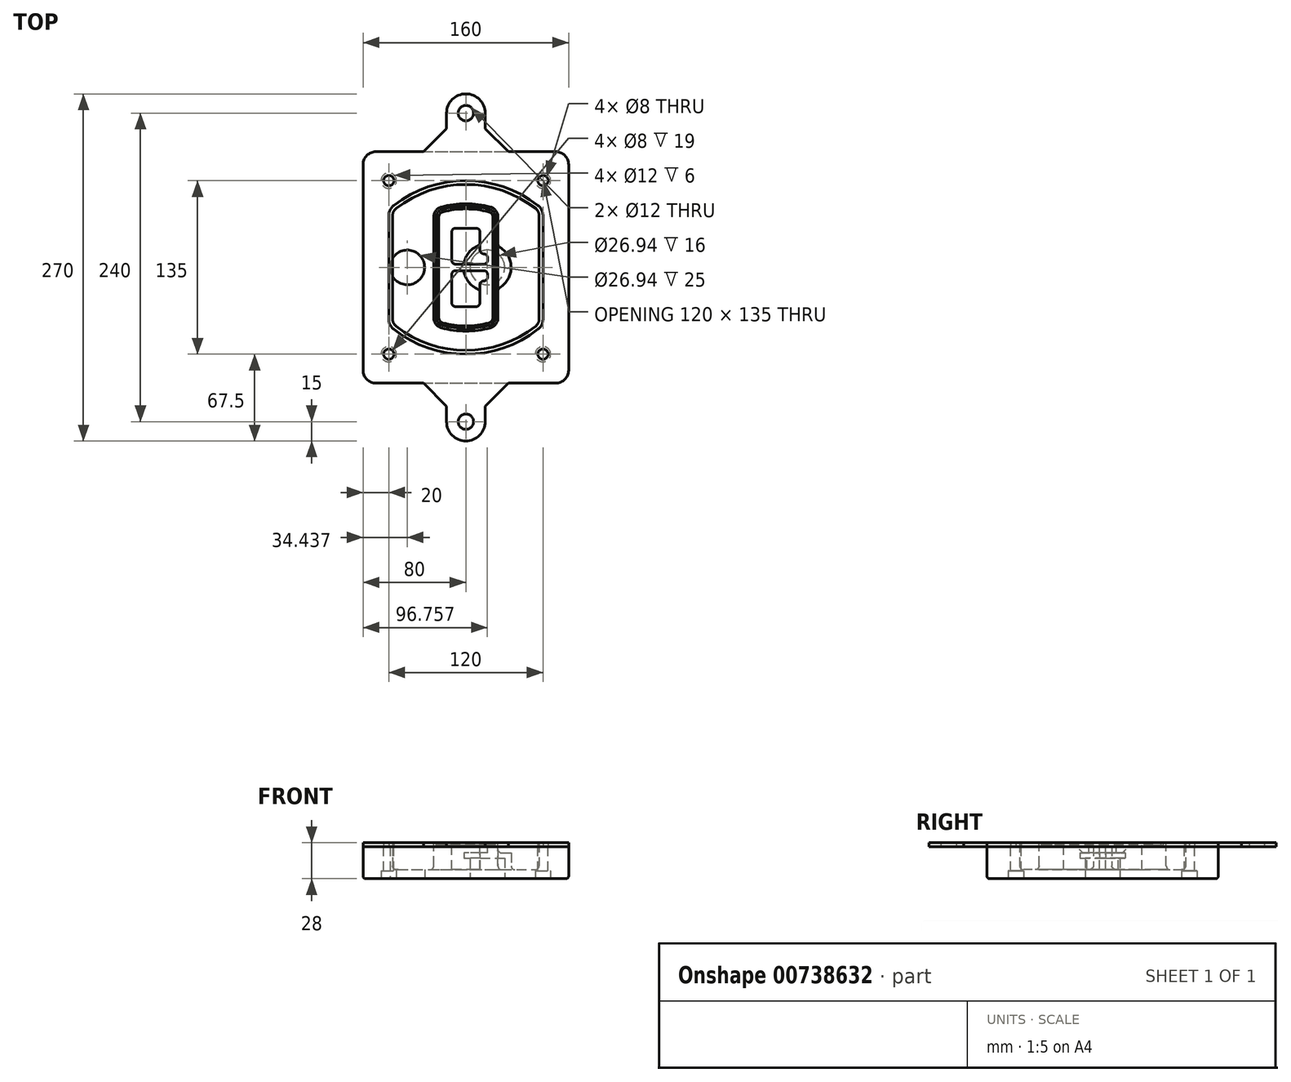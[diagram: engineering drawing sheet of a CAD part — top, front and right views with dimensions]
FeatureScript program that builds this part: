
annotation { "Feature Type Name" : "Feature", "Feature Type Description" : "" }
export const myFeature = defineFeature(function(context is Context, id is Id, definition is map)
    precondition{}
    {
        {
            var Q0;
            Q0=qCreatedBy(makeId("Top.planeOp"),FACE);
            var sketch = newSketch(context, id + "F0", { "sketchPlane" : qUnion([Q0])});
            skPoint(sketch, "E0.rect.middle", {"position": v(0, 0) * mm});
            skLineSegment(sketch, "E1.bottom", {"start": v(-70, -90) * mm, "end": v(70, -90) * mm});
            skLineSegment(sketch, "E1.top", {"start": v(-70, 90) * mm, "end": v(70, 90) * mm});
            skLineSegment(sketch, "E1.left", {"start": v(-80, -80) * mm, "end": v(-80, 80) * mm});
            skLineSegment(sketch, "E1.right", {"start": v(80, -80) * mm, "end": v(80, 80) * mm});
            skLineSegment(sketch, "E2", {"start": v(-80, 90) * mm, "end": v(80, -90) * mm, "construction": true});
            skLineSegment(sketch, "E3", {"start": v(80, 90) * mm, "end": v(-80, -90) * mm, "construction": true});
            skCircle(sketch, "E4", {"center": v(-60, 67.5) * mm, "radius": 4 * mm});
            skCircle(sketch, "E5", {"center": v(60, 67.5) * mm, "radius": 4 * mm});
            skCircle(sketch, "E6", {"center": v(60, -67.5) * mm, "radius": 4 * mm});
            skCircle(sketch, "E7", {"center": v(-60, -67.5) * mm, "radius": 4 * mm});
            skLineSegment(sketch, "E8", {"start": v(-60, 67.5) * mm, "end": v(60, 67.5) * mm, "construction": true});
            skLineSegment(sketch, "E9", {"start": v(60, 67.5) * mm, "end": v(60, -67.5) * mm, "construction": true});
            skLineSegment(sketch, "E10", {"start": v(60, -67.5) * mm, "end": v(-60, -67.5) * mm, "construction": true});
            skLineSegment(sketch, "E11", {"start": v(-60, -67.5) * mm, "end": v(-60, 67.5) * mm, "construction": true});
            skLineSegment(sketch, "E12", {"start": v(-60, 40.3) * mm, "end": v(-60, -40.3) * mm});
            skLineSegment(sketch, "E13", {"start": v(60, 40.3) * mm, "end": v(60, -40.3) * mm});
            skArc(sketch, "E14", {"start": v(56.15, 48.18) * mm, "mid": v(0, 67.5) * mm, "end": v(-56.15, 48.18) * mm});
            skArc(sketch, "E15", {"start": v(-56.15, -48.18) * mm, "mid": v(0, -67.5) * mm, "end": v(56.15, -48.18) * mm});
            skLineSegment(sketch, "E16", {"start": v(-60, 0) * mm, "end": v(60, 0) * mm, "construction": true});
            skPoint(sketch, "E17.visualSharp", {"position": v(-60, -45) * mm});
            skArc(sketch, "E17.filletArc", {"start": v(-60, -40.3) * mm, "mid": v(-58.99, -44.68) * mm, "end": v(-56.15, -48.18) * mm});
            skPoint(sketch, "E18.visualSharp", {"position": v(-60, 45) * mm});
            skArc(sketch, "E18.filletArc", {"start": v(-56.15, 48.18) * mm, "mid": v(-58.99, 44.68) * mm, "end": v(-60, 40.3) * mm});
            skPoint(sketch, "E19.visualSharp", {"position": v(60, 45) * mm});
            skArc(sketch, "E19.filletArc", {"start": v(60, 40.3) * mm, "mid": v(58.99, 44.68) * mm, "end": v(56.15, 48.18) * mm});
            skPoint(sketch, "E20.visualSharp", {"position": v(60, -45) * mm});
            skArc(sketch, "E20.filletArc", {"start": v(56.15, -48.18) * mm, "mid": v(58.99, -44.68) * mm, "end": v(60, -40.3) * mm});
            skPoint(sketch, "E21.visualSharp", {"position": v(-80, 90) * mm});
            skArc(sketch, "E21.filletArc", {"start": v(-70, 90) * mm, "mid": v(-77.07, 87.07) * mm, "end": v(-80, 80) * mm});
            skPoint(sketch, "E22.visualSharp", {"position": v(80, 90) * mm});
            skArc(sketch, "E22.filletArc", {"start": v(80, 80) * mm, "mid": v(77.07, 87.07) * mm, "end": v(70, 90) * mm});
            skPoint(sketch, "E23.visualSharp", {"position": v(80, -90) * mm});
            skArc(sketch, "E23.filletArc", {"start": v(70, -90) * mm, "mid": v(77.07, -87.07) * mm, "end": v(80, -80) * mm});
            skPoint(sketch, "E24.visualSharp", {"position": v(-80, -90) * mm});
            skArc(sketch, "E24.filletArc", {"start": v(-80, -80) * mm, "mid": v(-77.07, -87.07) * mm, "end": v(-70, -90) * mm});
            skArc(sketch, "E25.0", {"start": v(57, 40.3) * mm, "mid": v(56.3, 43.36) * mm, "end": v(54.3, 45.81) * mm});
            skLineSegment(sketch, "E25.1", {"start": v(57, 40.3) * mm, "end": v(57, -40.3) * mm});
            skArc(sketch, "E25.2", {"start": v(54.3, -45.81) * mm, "mid": v(56.3, -43.36) * mm, "end": v(57, -40.3) * mm});
            skArc(sketch, "E25.3", {"start": v(-54.3, -45.81) * mm, "mid": v(0, -64.5) * mm, "end": v(54.3, -45.81) * mm});
            skArc(sketch, "E25.4", {"start": v(-57, -40.3) * mm, "mid": v(-56.3, -43.36) * mm, "end": v(-54.3, -45.81) * mm});
            skArc(sketch, "E25.5", {"start": v(54.3, 45.81) * mm, "mid": v(0, 64.5) * mm, "end": v(-54.3, 45.81) * mm});
            skLineSegment(sketch, "E25.6", {"start": v(-57, 40.3) * mm, "end": v(-57, -40.3) * mm});
            skArc(sketch, "E25.7", {"start": v(-54.3, 45.81) * mm, "mid": v(-56.3, 43.36) * mm, "end": v(-57, 40.3) * mm});
            skArc(sketch, "E26.0", {"start": v(-58.62, 51.33) * mm, "mid": v(-62.58, 46.43) * mm, "end": v(-64, 40.3) * mm});
            skArc(sketch, "E26.1", {"start": v(58.62, 51.33) * mm, "mid": v(0, 71.5) * mm, "end": v(-58.62, 51.33) * mm});
            skArc(sketch, "E26.2", {"start": v(64, 40.3) * mm, "mid": v(62.58, 46.43) * mm, "end": v(58.62, 51.33) * mm});
            skLineSegment(sketch, "E26.3", {"start": v(64, 40.3) * mm, "end": v(64, -40.3) * mm});
            skArc(sketch, "E26.4", {"start": v(58.62, -51.33) * mm, "mid": v(62.58, -46.43) * mm, "end": v(64, -40.3) * mm});
            skLineSegment(sketch, "E26.5", {"start": v(-64, 40.3) * mm, "end": v(-64, -40.3) * mm});
            skArc(sketch, "E26.6", {"start": v(-58.62, -51.33) * mm, "mid": v(0, -71.5) * mm, "end": v(58.62, -51.33) * mm});
            skArc(sketch, "E26.7", {"start": v(-64, -40.3) * mm, "mid": v(-62.58, -46.43) * mm, "end": v(-58.62, -51.33) * mm});
            skSolve(sketch);
        }
        {
            var Q0;
            Q0=makeQuery(id+"F0.imprint","IMPRINT",FACE,{"disambiguationData":[TD([[makeQuery(id+"F0.imprint","IMPRINT",EDGE,{"derivedFrom":sQuery(id+"F0.wireOp",EDGE,"E1.bottom")}),1.0]])]});
            var Q1;
            Q1=makeQuery(id+"F0.imprint","IMPRINT",FACE,{"disambiguationData":[TD([[makeQuery(id+"F0.imprint","IMPRINT",EDGE,{"derivedFrom":sQuery(id+"F0.wireOp",EDGE,"E12")}),1.0]])]});
            var Q2;
            Q2=makeQuery(id+"F0.imprint","IMPRINT",FACE,{"disambiguationData":[TD([[makeQuery(id+"F0.imprint","IMPRINT",EDGE,{"derivedFrom":sQuery(id+"F0.wireOp",EDGE,"E25.0")}),1.0]])]});
            var Q3;
            Q3=makeQuery(id+"F0.imprint","IMPRINT",FACE,{"disambiguationData":[TD([[makeQuery(id+"F0.imprint","IMPRINT",EDGE,{"derivedFrom":sQuery(id+"F0.wireOp",EDGE,"E12")}),-1.0]])]});
            extrude(context, id + "F1", {"entities" : qUnion([Q0, Q1, Q2, Q3]), "oppositeDirection" : true, "depth" : 25 * mm});
        }
        {
            var Q0;
            Q0=makeQuery(id+"F0.imprint","IMPRINT",FACE,{"disambiguationData":[TD([[makeQuery(id+"F0.imprint","IMPRINT",EDGE,{"derivedFrom":sQuery(id+"F0.wireOp",EDGE,"E12")}),1.0]])]});
            extrude(context, id + "F2", {"entities" : qUnion([Q0]), "operationType" : NewBodyOperationType.ADD, "depth" : 3 * mm});
        }
        {
            var Q0;
            Q0=makeQuery(id+"F0.imprint","IMPRINT",FACE,{"disambiguationData":[TD([[makeQuery(id+"F0.imprint","IMPRINT",EDGE,{"derivedFrom":sQuery(id+"F0.wireOp",EDGE,"E25.0")}),1.0]])]});
            extrude(context, id + "F3", {"entities" : qUnion([Q0]), "operationType" : NewBodyOperationType.REMOVE, "oppositeDirection" : true, "depth" : 18 * mm});
        }
        {
            var Q0;
            Q0=makeQuery(id+"F2.opExtrude","CAP_FACE",FACE,{"disambiguationData":[OSD([sQuery(id+"F0.wireOp",EDGE,"E12"),sQuery(id+"F0.wireOp",EDGE,"E13"),sQuery(id+"F0.wireOp",EDGE,"E14"),sQuery(id+"F0.wireOp",EDGE,"E15"),sQuery(id+"F0.wireOp",EDGE,"E17.filletArc"),sQuery(id+"F0.wireOp",EDGE,"E18.filletArc"),sQuery(id+"F0.wireOp",EDGE,"E19.filletArc"),sQuery(id+"F0.wireOp",EDGE,"E20.filletArc"),sQuery(id+"F0.wireOp",EDGE,"E25.0"),sQuery(id+"F0.wireOp",EDGE,"E25.1"),sQuery(id+"F0.wireOp",EDGE,"E25.2"),sQuery(id+"F0.wireOp",EDGE,"E25.3"),sQuery(id+"F0.wireOp",EDGE,"E25.4"),sQuery(id+"F0.wireOp",EDGE,"E25.5"),sQuery(id+"F0.wireOp",EDGE,"E25.6"),sQuery(id+"F0.wireOp",EDGE,"E25.7")])],"isStart":false});
            var sketch = newSketch(context, id + "F4", { "sketchPlane" : qUnion([Q0])});
            skArc(sketch, "E27.0", {"start": v(-19.08, -46.97) * mm, "mid": v(0, -49.5) * mm, "end": v(19.08, -46.97) * mm});
            skArc(sketch, "E28.0", {"start": v(19.08, 46.97) * mm, "mid": v(0, 49.5) * mm, "end": v(-19.08, 46.97) * mm});
            skLineSegment(sketch, "E29", {"start": v(-25, 39.25) * mm, "end": v(-25, -39.25) * mm});
            skLineSegment(sketch, "E30", {"start": v(25, 39.25) * mm, "end": v(25, -39.25) * mm});
            skLineSegment(sketch, "E31", {"start": v(-25, 45.1) * mm, "end": v(25, 45.1) * mm, "construction": true});
            skLineSegment(sketch, "E32", {"start": v(-25, -45.1) * mm, "end": v(25, -45.1) * mm, "construction": true});
            skPoint(sketch, "E33.visualSharp", {"position": v(-25, 45.1) * mm});
            skArc(sketch, "E33.filletArc", {"start": v(-19.08, 46.97) * mm, "mid": v(-23.35, 44.11) * mm, "end": v(-25, 39.25) * mm});
            skPoint(sketch, "E34.visualSharp", {"position": v(25, 45.1) * mm});
            skArc(sketch, "E34.filletArc", {"start": v(25, 39.25) * mm, "mid": v(23.35, 44.11) * mm, "end": v(19.08, 46.97) * mm});
            skPoint(sketch, "E35.visualSharp", {"position": v(25, -45.1) * mm});
            skArc(sketch, "E35.filletArc", {"start": v(19.08, -46.97) * mm, "mid": v(23.35, -44.11) * mm, "end": v(25, -39.25) * mm});
            skPoint(sketch, "E36.visualSharp", {"position": v(-25, -45.1) * mm});
            skArc(sketch, "E36.filletArc", {"start": v(-25, -39.25) * mm, "mid": v(-23.35, -44.11) * mm, "end": v(-19.08, -46.97) * mm});
            skArc(sketch, "E37.0", {"start": v(54.3, 45.81) * mm, "mid": v(0, 64.5) * mm, "end": v(-54.3, 45.81) * mm});
            skArc(sketch, "E37.1", {"start": v(-54.3, 45.81) * mm, "mid": v(-56.3, 43.36) * mm, "end": v(-57, 40.3) * mm});
            skLineSegment(sketch, "E37.2", {"start": v(-57, 40.3) * mm, "end": v(-57, -40.3) * mm});
            skArc(sketch, "E37.3", {"start": v(-57, -40.3) * mm, "mid": v(-56.3, -43.36) * mm, "end": v(-54.3, -45.81) * mm});
            skArc(sketch, "E37.4", {"start": v(-54.3, -45.81) * mm, "mid": v(0, -64.5) * mm, "end": v(54.3, -45.81) * mm});
            skArc(sketch, "E37.5", {"start": v(54.3, -45.81) * mm, "mid": v(56.3, -43.36) * mm, "end": v(57, -40.3) * mm});
            skLineSegment(sketch, "E37.6", {"start": v(57, 40.3) * mm, "end": v(57, -40.3) * mm});
            skArc(sketch, "E37.7", {"start": v(57, 40.3) * mm, "mid": v(56.3, 43.36) * mm, "end": v(54.3, 45.81) * mm});
            skLineSegment(sketch, "E38.0", {"start": v(23, 39.25) * mm, "end": v(23, -39.25) * mm});
            skArc(sketch, "E38.1", {"start": v(18.56, -45.04) * mm, "mid": v(21.76, -42.9) * mm, "end": v(23, -39.25) * mm});
            skArc(sketch, "E38.2", {"start": v(-18.56, -45.04) * mm, "mid": v(0, -47.5) * mm, "end": v(18.56, -45.04) * mm});
            skArc(sketch, "E38.3", {"start": v(-23, -39.25) * mm, "mid": v(-21.76, -42.9) * mm, "end": v(-18.56, -45.04) * mm});
            skLineSegment(sketch, "E38.4", {"start": v(-23, 39.25) * mm, "end": v(-23, -39.25) * mm});
            skArc(sketch, "E38.5", {"start": v(23, 39.25) * mm, "mid": v(21.76, 42.9) * mm, "end": v(18.56, 45.04) * mm});
            skArc(sketch, "E38.6", {"start": v(-18.56, 45.04) * mm, "mid": v(-21.76, 42.9) * mm, "end": v(-23, 39.25) * mm});
            skArc(sketch, "E38.7", {"start": v(18.56, 45.04) * mm, "mid": v(0, 47.5) * mm, "end": v(-18.56, 45.04) * mm});
            skArc(sketch, "E39.0", {"start": v(21, 39.25) * mm, "mid": v(20.18, 41.68) * mm, "end": v(18.04, 43.1) * mm});
            skLineSegment(sketch, "E39.1", {"start": v(21, 39.25) * mm, "end": v(21, -39.25) * mm});
            skArc(sketch, "E39.2", {"start": v(18.04, -43.1) * mm, "mid": v(20.18, -41.68) * mm, "end": v(21, -39.25) * mm});
            skArc(sketch, "E39.3", {"start": v(-18.04, -43.1) * mm, "mid": v(0, -45.5) * mm, "end": v(18.04, -43.1) * mm});
            skArc(sketch, "E39.4", {"start": v(-21, -39.25) * mm, "mid": v(-20.18, -41.68) * mm, "end": v(-18.04, -43.1) * mm});
            skArc(sketch, "E39.5", {"start": v(18.04, 43.1) * mm, "mid": v(0, 45.5) * mm, "end": v(-18.04, 43.1) * mm});
            skLineSegment(sketch, "E39.6", {"start": v(-21, 39.25) * mm, "end": v(-21, -39.25) * mm});
            skArc(sketch, "E39.7", {"start": v(-18.04, 43.1) * mm, "mid": v(-20.18, 41.68) * mm, "end": v(-21, 39.25) * mm});
            skLineSegment(sketch, "E40", {"start": v(-25, 0) * mm, "end": v(25, 0) * mm, "construction": true});
            skLineSegment(sketch, "E41", {"start": v(-11, 5.5) * mm, "end": v(-11, 27.5) * mm});
            skLineSegment(sketch, "E42", {"start": v(-8, 30.5) * mm, "end": v(8, 30.5) * mm});
            skLineSegment(sketch, "E43", {"start": v(11, 27.5) * mm, "end": v(11, 13.5) * mm});
            skLineSegment(sketch, "E44", {"start": v(14, 10.5) * mm, "end": v(14, 10.5) * mm});
            skLineSegment(sketch, "E45", {"start": v(17, 7.5) * mm, "end": v(17, 5.5) * mm});
            skLineSegment(sketch, "E46", {"start": v(14, 2.5) * mm, "end": v(-8, 2.5) * mm});
            skPoint(sketch, "E47.visualSharp", {"position": v(-11, 30.5) * mm});
            skArc(sketch, "E47.filletArc", {"start": v(-8, 30.5) * mm, "mid": v(-10.12, 29.62) * mm, "end": v(-11, 27.5) * mm});
            skPoint(sketch, "E48.visualSharp", {"position": v(11, 30.5) * mm});
            skArc(sketch, "E48.filletArc", {"start": v(11, 27.5) * mm, "mid": v(10.12, 29.62) * mm, "end": v(8, 30.5) * mm});
            skPoint(sketch, "E49.visualSharp", {"position": v(11, 10.5) * mm});
            skArc(sketch, "E49.filletArc", {"start": v(11, 13.5) * mm, "mid": v(11.88, 11.38) * mm, "end": v(14, 10.5) * mm});
            skPoint(sketch, "E50.visualSharp", {"position": v(17, 10.5) * mm});
            skArc(sketch, "E50.filletArc", {"start": v(17, 7.5) * mm, "mid": v(16.12, 9.62) * mm, "end": v(14, 10.5) * mm});
            skPoint(sketch, "E51.visualSharp", {"position": v(17, 2.5) * mm});
            skArc(sketch, "E51.filletArc", {"start": v(14, 2.5) * mm, "mid": v(16.12, 3.38) * mm, "end": v(17, 5.5) * mm});
            skPoint(sketch, "E52.visualSharp", {"position": v(-11, 2.5) * mm});
            skArc(sketch, "E52.filletArc", {"start": v(-11, 5.5) * mm, "mid": v(-10.12, 3.38) * mm, "end": v(-8, 2.5) * mm});
            skLineSegment(sketch, "E53.0.MirrorCS", {"start": v(14, -2.5) * mm, "end": v(-8, -2.5) * mm});
            skArc(sketch, "E54.0.MirrorCS", {"start": v(-11, -5.5) * mm, "mid": v(-10.12, -3.38) * mm, "end": v(-8, -2.5) * mm});
            skLineSegment(sketch, "E55.0.MirrorCS", {"start": v(-11, -5.5) * mm, "end": v(-11, -27.5) * mm});
            skArc(sketch, "E56.0.MirrorCS", {"start": v(-8, -30.5) * mm, "mid": v(-10.12, -29.62) * mm, "end": v(-11, -27.5) * mm});
            skLineSegment(sketch, "E57.0.MirrorCS", {"start": v(-8, -30.5) * mm, "end": v(8, -30.5) * mm});
            skArc(sketch, "E58.0.MirrorCS", {"start": v(11, -27.5) * mm, "mid": v(10.12, -29.62) * mm, "end": v(8, -30.5) * mm});
            skLineSegment(sketch, "E59.0.MirrorCS", {"start": v(11, -27.5) * mm, "end": v(11, -13.5) * mm});
            skArc(sketch, "E60.0.MirrorCS", {"start": v(11, -13.5) * mm, "mid": v(11.88, -11.38) * mm, "end": v(14, -10.5) * mm});
            skArc(sketch, "E61.0.MirrorCS", {"start": v(17, -7.5) * mm, "mid": v(16.12, -9.62) * mm, "end": v(14, -10.5) * mm});
            skLineSegment(sketch, "E62.0.MirrorCS", {"start": v(17, -7.5) * mm, "end": v(17, -5.5) * mm});
            skArc(sketch, "E63.0.MirrorCS", {"start": v(14, -2.5) * mm, "mid": v(16.12, -3.38) * mm, "end": v(17, -5.5) * mm});
            skSolve(sketch);
        }
        {
            var Q0;
            Q0=makeQuery(id+"F4.imprint","IMPRINT",FACE,{"disambiguationData":[TD([[makeQuery(id+"F4.imprint","IMPRINT",EDGE,{"derivedFrom":sQuery(id+"F4.wireOp",EDGE,"E27.0")}),1.0]])]});
            var Q1;
            Q1=makeQuery(id+"F4.imprint","IMPRINT",FACE,{"disambiguationData":[TD([[makeQuery(id+"F4.imprint","IMPRINT",EDGE,{"derivedFrom":sQuery(id+"F4.wireOp",EDGE,"E38.0")}),-1.0]])]});
            var Q2;
            Q2=makeQuery(id+"F4.imprint","IMPRINT",FACE,{"disambiguationData":[TD([[makeQuery(id+"F4.imprint","IMPRINT",EDGE,{"derivedFrom":sQuery(id+"F4.wireOp",EDGE,"E39.0")}),1.0]])]});
            extrude(context, id + "F5", {"entities" : qUnion([Q0, Q1, Q2]), "operationType" : NewBodyOperationType.ADD, "endBound" : BoundingType.UP_TO_NEXT, "oppositeDirection" : true, "depth" : 25 * mm});
        }
        {
            var Q0;
            Q0=makeQuery(id+"F4.imprint","IMPRINT",FACE,{"disambiguationData":[TD([[makeQuery(id+"F4.imprint","IMPRINT",EDGE,{"derivedFrom":sQuery(id+"F4.wireOp",EDGE,"E38.0")}),-1.0]])]});
            extrude(context, id + "F6", {"entities" : qUnion([Q0]), "operationType" : NewBodyOperationType.REMOVE, "oppositeDirection" : true, "depth" : 2 * mm});
        }
        {
            var Q0;
            Q0=makeQuery(id+"F1.opExtrude","CAP_FACE",FACE,{"disambiguationData":[OSD([sQuery(id+"F0.wireOp",EDGE,"E1.bottom"),sQuery(id+"F0.wireOp",EDGE,"E1.top"),sQuery(id+"F0.wireOp",EDGE,"E1.left"),sQuery(id+"F0.wireOp",EDGE,"E1.right"),sQuery(id+"F0.wireOp",EDGE,"E4"),sQuery(id+"F0.wireOp",EDGE,"E5"),sQuery(id+"F0.wireOp",EDGE,"E6"),sQuery(id+"F0.wireOp",EDGE,"E7"),sQuery(id+"F0.wireOp",EDGE,"E21.filletArc"),sQuery(id+"F0.wireOp",EDGE,"E22.filletArc"),sQuery(id+"F0.wireOp",EDGE,"E23.filletArc"),sQuery(id+"F0.wireOp",EDGE,"E24.filletArc")])],"isStart":false});
            var sketch = newSketch(context, id + "F7", { "sketchPlane" : qUnion([Q0])});
            skCircle(sketch, "E64", {"center": v(16.76, 0) * mm, "radius": 13.47 * mm});
            skCircle(sketch, "E65", {"center": v(-45.56, 0) * mm, "radius": 13.47 * mm});
            skLineSegment(sketch, "E66", {"start": v(80, 0) * mm, "end": v(-80, 0) * mm});
            skCircle(sketch, "E67", {"center": v(16.76, 0) * mm, "radius": 18.47 * mm});
            skCircle(sketch, "E68", {"center": v(60, -67.5) * mm, "radius": 6 * mm});
            skCircle(sketch, "E69", {"center": v(-60, -67.5) * mm, "radius": 6 * mm});
            skCircle(sketch, "E70", {"center": v(-60, 67.5) * mm, "radius": 6 * mm});
            skCircle(sketch, "E71", {"center": v(60, 67.5) * mm, "radius": 6 * mm});
            skSolve(sketch);
        }
        {
            var Q0;
            {var subQ1=sQuery(id+"F7.wireOp",EDGE,"E66");var subQ4=sQuery(id+"F7.wireOp",EDGE,"E64");var subQ6=makeQuery(id+"F7.imprint","INTERSECT",VERTEX,{"disambiguationData":[OD(0.0)],"derivedFrom":[subQ4,subQ1]});Q0=makeQuery(id+"F7.imprint","IMPRINT",FACE,{"disambiguationData":[TD([[makeQuery(id+"F7.imprint","IMPRINT",EDGE,{"disambiguationData":[TD([[subQ6,-1.0]])],"derivedFrom":subQ4}),-1.0]])]});}
            var Q1;
            {var subQ0=sQuery(id+"F7.wireOp",EDGE,"E66");var subQ1=sQuery(id+"F7.wireOp",EDGE,"E64");var subQ3=makeQuery(id+"F7.imprint","INTERSECT",VERTEX,{"disambiguationData":[OD(0.0)],"derivedFrom":[subQ1,subQ0]});Q1=makeQuery(id+"F7.imprint","IMPRINT",FACE,{"disambiguationData":[TD([[makeQuery(id+"F7.imprint","IMPRINT",EDGE,{"disambiguationData":[TD([[subQ3,-1.0]])],"derivedFrom":subQ1}),1.0]])]});}
            var Q2;
            {var subQ0=sQuery(id+"F7.wireOp",EDGE,"E66");var subQ1=sQuery(id+"F7.wireOp",EDGE,"E64");var subQ3=makeQuery(id+"F7.imprint","INTERSECT",VERTEX,{"disambiguationData":[OD(0.0)],"derivedFrom":[subQ1,subQ0]});Q2=makeQuery(id+"F7.imprint","IMPRINT",FACE,{"disambiguationData":[TD([[makeQuery(id+"F7.imprint","IMPRINT",EDGE,{"disambiguationData":[TD([[subQ3,1.0]])],"derivedFrom":subQ1}),1.0]])]});}
            var Q3;
            {var subQ1=sQuery(id+"F7.wireOp",EDGE,"E66");var subQ4=sQuery(id+"F7.wireOp",EDGE,"E64");var subQ6=makeQuery(id+"F7.imprint","INTERSECT",VERTEX,{"disambiguationData":[OD(0.0)],"derivedFrom":[subQ4,subQ1]});Q3=makeQuery(id+"F7.imprint","IMPRINT",FACE,{"disambiguationData":[TD([[makeQuery(id+"F7.imprint","IMPRINT",EDGE,{"disambiguationData":[TD([[subQ6,1.0]])],"derivedFrom":subQ4}),-1.0]])]});}
            extrude(context, id + "F8", {"entities" : qUnion([Q0, Q1, Q2, Q3]), "operationType" : NewBodyOperationType.ADD, "oppositeDirection" : true, "depth" : 20 * mm});
        }
        {
            var Q0;
            {var subQ0=sQuery(id+"F7.wireOp",EDGE,"E66");var subQ1=sQuery(id+"F7.wireOp",EDGE,"E64");var subQ3=makeQuery(id+"F7.imprint","INTERSECT",VERTEX,{"disambiguationData":[OD(0.0)],"derivedFrom":[subQ1,subQ0]});Q0=makeQuery(id+"F7.imprint","IMPRINT",FACE,{"disambiguationData":[TD([[makeQuery(id+"F7.imprint","IMPRINT",EDGE,{"disambiguationData":[TD([[subQ3,-1.0]])],"derivedFrom":subQ1}),1.0]])]});}
            var Q1;
            {var subQ0=sQuery(id+"F7.wireOp",EDGE,"E66");var subQ1=sQuery(id+"F7.wireOp",EDGE,"E64");var subQ3=makeQuery(id+"F7.imprint","INTERSECT",VERTEX,{"disambiguationData":[OD(0.0)],"derivedFrom":[subQ1,subQ0]});Q1=makeQuery(id+"F7.imprint","IMPRINT",FACE,{"disambiguationData":[TD([[makeQuery(id+"F7.imprint","IMPRINT",EDGE,{"disambiguationData":[TD([[subQ3,1.0]])],"derivedFrom":subQ1}),1.0]])]});}
            extrude(context, id + "F9", {"entities" : qUnion([Q0, Q1]), "operationType" : NewBodyOperationType.REMOVE, "oppositeDirection" : true, "depth" : 16 * mm});
        }
        {
            var Q0;
            {var subQ0=sQuery(id+"F7.wireOp",EDGE,"E66");var subQ1=sQuery(id+"F7.wireOp",EDGE,"E65");var subQ3=makeQuery(id+"F7.imprint","INTERSECT",VERTEX,{"disambiguationData":[OD(0.0)],"derivedFrom":[subQ1,subQ0]});Q0=makeQuery(id+"F7.imprint","IMPRINT",FACE,{"disambiguationData":[TD([[makeQuery(id+"F7.imprint","IMPRINT",EDGE,{"disambiguationData":[TD([[subQ3,-1.0]])],"derivedFrom":subQ1}),1.0]])]});}
            var Q1;
            {var subQ0=sQuery(id+"F7.wireOp",EDGE,"E66");var subQ1=sQuery(id+"F7.wireOp",EDGE,"E65");var subQ3=makeQuery(id+"F7.imprint","INTERSECT",VERTEX,{"disambiguationData":[OD(0.0)],"derivedFrom":[subQ1,subQ0]});Q1=makeQuery(id+"F7.imprint","IMPRINT",FACE,{"disambiguationData":[TD([[makeQuery(id+"F7.imprint","IMPRINT",EDGE,{"disambiguationData":[TD([[subQ3,1.0]])],"derivedFrom":subQ1}),1.0]])]});}
            extrude(context, id + "F10", {"entities" : qUnion([Q0, Q1]), "operationType" : NewBodyOperationType.REMOVE, "oppositeDirection" : true, "depth" : 25 * mm});
        }
        {
            var Q0;
            Q0=makeQuery(id+"F7.imprint","IMPRINT",FACE,{"disambiguationData":[TD([[makeQuery(id+"F7.imprint","IMPRINT",EDGE,{"derivedFrom":sQuery(id+"F7.wireOp",EDGE,"E68")}),1.0]])]});
            var Q1;
            Q1=makeQuery(id+"F7.imprint","IMPRINT",FACE,{"disambiguationData":[TD([[makeQuery(id+"F7.imprint","IMPRINT",EDGE,{"derivedFrom":makeQuery(id+"F1.opExtrude","CAP_EDGE",EDGE,{"disambiguationData":[OSD([sQuery(id+"F0.wireOp",EDGE,"E5")])],"isStart":false})}),-1.0]])]});
            var Q2;
            Q2=makeQuery(id+"F7.imprint","IMPRINT",FACE,{"disambiguationData":[TD([[makeQuery(id+"F7.imprint","IMPRINT",EDGE,{"derivedFrom":sQuery(id+"F7.wireOp",EDGE,"E69")}),1.0]])]});
            var Q3;
            Q3=makeQuery(id+"F7.imprint","IMPRINT",FACE,{"disambiguationData":[TD([[makeQuery(id+"F7.imprint","IMPRINT",EDGE,{"derivedFrom":makeQuery(id+"F1.opExtrude","CAP_EDGE",EDGE,{"disambiguationData":[OSD([sQuery(id+"F0.wireOp",EDGE,"E4")])],"isStart":false})}),-1.0]])]});
            var Q4;
            Q4=makeQuery(id+"F7.imprint","IMPRINT",FACE,{"disambiguationData":[TD([[makeQuery(id+"F7.imprint","IMPRINT",EDGE,{"derivedFrom":sQuery(id+"F7.wireOp",EDGE,"E70")}),1.0]])]});
            var Q5;
            Q5=makeQuery(id+"F7.imprint","IMPRINT",FACE,{"disambiguationData":[TD([[makeQuery(id+"F7.imprint","IMPRINT",EDGE,{"derivedFrom":makeQuery(id+"F1.opExtrude","CAP_EDGE",EDGE,{"disambiguationData":[OSD([sQuery(id+"F0.wireOp",EDGE,"E7")])],"isStart":false})}),-1.0]])]});
            var Q6;
            Q6=makeQuery(id+"F7.imprint","IMPRINT",FACE,{"disambiguationData":[TD([[makeQuery(id+"F7.imprint","IMPRINT",EDGE,{"derivedFrom":sQuery(id+"F7.wireOp",EDGE,"E71")}),1.0]])]});
            var Q7;
            Q7=makeQuery(id+"F7.imprint","IMPRINT",FACE,{"disambiguationData":[TD([[makeQuery(id+"F7.imprint","IMPRINT",EDGE,{"derivedFrom":makeQuery(id+"F1.opExtrude","CAP_EDGE",EDGE,{"disambiguationData":[OSD([sQuery(id+"F0.wireOp",EDGE,"E6")])],"isStart":false})}),-1.0]])]});
            extrude(context, id + "F11", {"entities" : qUnion([Q0, Q1, Q2, Q3, Q4, Q5, Q6, Q7]), "operationType" : NewBodyOperationType.REMOVE, "oppositeDirection" : true, "depth" : 6 * mm});
        }
        {
            var Q0;
            Q0=makeQuery(id+"F9.boolean.opBoolean","COPY",FACE,{"derivedFrom":makeQuery(id+"F9.opExtrude","CAP_FACE",FACE,{"disambiguationData":[OSD([sQuery(id+"F7.wireOp",EDGE,"E64")])],"isStart":false})});
            var sketch = newSketch(context, id + "F12", { "sketchPlane" : qUnion([Q0])});
            skArc(sketch, "E72.0", {"start": v(11, 17.55) * mm, "mid": v(2.57, 11.82) * mm, "end": v(-1.54, 2.5) * mm});
            skArc(sketch, "E72.1", {"start": v(-1.54, -2.5) * mm, "mid": v(2.57, -11.82) * mm, "end": v(11, -17.55) * mm});
            skLineSegment(sketch, "E73", {"start": v(-1.54, -2.5) * mm, "end": v(14, -2.5) * mm});
            skLineSegment(sketch, "E74.0", {"start": v(14, 2.5) * mm, "end": v(-1.54, 2.5) * mm});
            skArc(sketch, "E74.1", {"start": v(14, 2.5) * mm, "mid": v(16.12, 3.38) * mm, "end": v(17, 5.5) * mm});
            skLineSegment(sketch, "E74.2", {"start": v(17, 7.5) * mm, "end": v(17, 5.5) * mm});
            skArc(sketch, "E74.3", {"start": v(17, 7.5) * mm, "mid": v(16.12, 9.62) * mm, "end": v(14, 10.5) * mm});
            skArc(sketch, "E74.4", {"start": v(11, 13.5) * mm, "mid": v(11.88, 11.38) * mm, "end": v(14, 10.5) * mm});
            skLineSegment(sketch, "E74.5", {"start": v(11, 17.55) * mm, "end": v(11, 13.5) * mm});
            skLineSegment(sketch, "E74.7", {"start": v(14, -2.5) * mm, "end": v(-1.54, -2.5) * mm});
            skArc(sketch, "E74.8", {"start": v(14, -2.5) * mm, "mid": v(16.12, -3.38) * mm, "end": v(17, -5.5) * mm});
            skLineSegment(sketch, "E74.9", {"start": v(17, -7.5) * mm, "end": v(17, -5.5) * mm});
            skArc(sketch, "E74.10", {"start": v(17, -7.5) * mm, "mid": v(16.12, -9.62) * mm, "end": v(14, -10.5) * mm});
            skArc(sketch, "E74.11", {"start": v(11, -13.5) * mm, "mid": v(11.88, -11.38) * mm, "end": v(14, -10.5) * mm});
            skLineSegment(sketch, "E74.12", {"start": v(11, -17.55) * mm, "end": v(11, -13.5) * mm});
            skPoint(sketch, "E75.orphan", {"position": v(11, -27.5) * mm});
            skPoint(sketch, "E76.orphan", {"position": v(-8, -2.5) * mm});
            skPoint(sketch, "E77.orphan", {"position": v(-8, 2.5) * mm});
            skPoint(sketch, "E78.orphan", {"position": v(11, 27.5) * mm});
            skSolve(sketch);
        }
        {
            var Q0;
            {var subQ7=sQuery(id+"F12.wireOp",EDGE,"E72.0");var subQ14=sQuery(id+"F12.wireOp",EDGE,"E72.1");var subQ16=sQuery(id+"F12.wireOp",EDGE,"E74.1");var subQ18=sQuery(id+"F12.wireOp",EDGE,"E74.8");Q0=qUnion([makeQuery(id+"F12.imprint","IMPRINT",FACE,{"disambiguationData":[TD([[makeQuery(id+"F12.imprint","IMPRINT",EDGE,{"derivedFrom":subQ7}),1.0]])]}),makeQuery(id+"F12.imprint","IMPRINT",FACE,{"disambiguationData":[TD([[makeQuery(id+"F12.imprint","IMPRINT",EDGE,{"derivedFrom":subQ14}),1.0]])]}),makeQuery(id+"F12.imprint","IMPRINT",FACE,{"disambiguationData":[TD([[makeQuery(id+"F12.imprint","IMPRINT",EDGE,{"derivedFrom":subQ16}),1.0]])]}),makeQuery(id+"F12.imprint","IMPRINT",FACE,{"disambiguationData":[TD([[makeQuery(id+"F12.imprint","IMPRINT",EDGE,{"derivedFrom":subQ18}),-1.0]])]})]);}
            var Q1;
            Q1=makeQuery(id+"F5.boolean.opBoolean","SPLIT",FACE,{"disambiguationData":[TD([makeQuery(id+"F5.opExtrude","SWEPT_FACE",FACE,{"disambiguationData":[OSD([sQuery(id+"F4.wireOp",EDGE,"E41")])]})])],"derivedFrom":makeQuery(id+"F3.boolean.opBoolean","COPY",FACE,{"derivedFrom":makeQuery(id+"F3.opExtrude","CAP_FACE",FACE,{"disambiguationData":[OSD([sQuery(id+"F0.wireOp",EDGE,"E25.0"),sQuery(id+"F0.wireOp",EDGE,"E25.1"),sQuery(id+"F0.wireOp",EDGE,"E25.2"),sQuery(id+"F0.wireOp",EDGE,"E25.3"),sQuery(id+"F0.wireOp",EDGE,"E25.4"),sQuery(id+"F0.wireOp",EDGE,"E25.5"),sQuery(id+"F0.wireOp",EDGE,"E25.6"),sQuery(id+"F0.wireOp",EDGE,"E25.7")])],"isStart":false})})});
            extrude(context, id + "F13", {"entities" : qUnion([Q0]), "operationType" : NewBodyOperationType.REMOVE, "endBound" : BoundingType.UP_TO_SURFACE, "endBoundEntityFace" : qUnion([Q1]), "depth" : 25 * mm});
        }
        {
            var Q0;
            Q0=makeQuery(id+"F3.boolean.opBoolean","COPY",EDGE,{"derivedFrom":makeQuery(id+"F3.opExtrude","CAP_EDGE",EDGE,{"disambiguationData":[OSD([sQuery(id+"F0.wireOp",EDGE,"E25.6")])],"isStart":false})});
            var Q1;
            Q1=makeQuery(id+"F8.boolean.opBoolean","INTERSECT",EDGE,{"derivedFrom":[makeQuery(id+"F5.opExtrude","SWEPT_FACE",FACE,{"disambiguationData":[OSD([sQuery(id+"F4.wireOp",EDGE,"E30")])]}),makeQuery(id+"F8.opExtrude","CAP_FACE",FACE,{"disambiguationData":[OSD([sQuery(id+"F7.wireOp",EDGE,"E67")])],"isStart":false})]});
            var Q2;
            Q2=makeQuery(id+"F8.boolean.opBoolean","INTERSECT",EDGE,{"disambiguationData":[OD(1.0)],"derivedFrom":[makeQuery(id+"F5.opExtrude","SWEPT_FACE",FACE,{"disambiguationData":[OSD([sQuery(id+"F4.wireOp",EDGE,"E30")])]}),makeQuery(id+"F8.opExtrude","SWEPT_FACE",FACE,{"disambiguationData":[OSD([sQuery(id+"F7.wireOp",EDGE,"E67")])]})]});
            var Q3;
            {var subQ0=sQuery(id+"F4.wireOp",EDGE,"E30");Q3=makeQuery(id+"F8.boolean.opBoolean","SPLIT",EDGE,{"disambiguationData":[TD([makeQuery(id+"F5.opExtrude","SWEPT_FACE",FACE,{"disambiguationData":[OSD([sQuery(id+"F4.wireOp",EDGE,"E35.filletArc")])]})])],"derivedFrom":makeQuery(id+"F5.opExtrude","CAP_EDGE",EDGE,{"disambiguationData":[OSD([subQ0])],"isStart":false})});}
            var Q4;
            {var subQ0=sQuery(id+"F0.wireOp",EDGE,"E25.7");var subQ1=sQuery(id+"F0.wireOp",EDGE,"E25.1");var subQ2=sQuery(id+"F0.wireOp",EDGE,"E25.6");var subQ3=sQuery(id+"F0.wireOp",EDGE,"E25.5");var subQ4=sQuery(id+"F0.wireOp",EDGE,"E25.4");var subQ5=sQuery(id+"F0.wireOp",EDGE,"E25.0");var subQ6=sQuery(id+"F0.wireOp",EDGE,"E25.2");var subQ7=sQuery(id+"F0.wireOp",EDGE,"E25.3");Q4=makeQuery(id+"F8.boolean.opBoolean","INTERSECT",EDGE,{"derivedFrom":[makeQuery(id+"F5.boolean.opBoolean","SPLIT",FACE,{"disambiguationData":[TD([makeQuery(id+"F2.opExtrude","SWEPT_FACE",FACE,{"disambiguationData":[OSD([subQ5])]})])],"derivedFrom":makeQuery(id+"F3.boolean.opBoolean","COPY",FACE,{"derivedFrom":makeQuery(id+"F3.opExtrude","CAP_FACE",FACE,{"disambiguationData":[OSD([subQ5,subQ1,subQ6,subQ7,subQ4,subQ3,subQ2,subQ0])],"isStart":false})})}),makeQuery(id+"F8.opExtrude","SWEPT_FACE",FACE,{"disambiguationData":[OSD([sQuery(id+"F7.wireOp",EDGE,"E67")])]})]});}
            var Q5;
            Q5=makeQuery(id+"F8.boolean.opBoolean","INTERSECT",EDGE,{"disambiguationData":[OD(0.0)],"derivedFrom":[makeQuery(id+"F5.opExtrude","SWEPT_FACE",FACE,{"disambiguationData":[OSD([sQuery(id+"F4.wireOp",EDGE,"E30")])]}),makeQuery(id+"F8.opExtrude","SWEPT_FACE",FACE,{"disambiguationData":[OSD([sQuery(id+"F7.wireOp",EDGE,"E67")])]})]});
            fillet(context, id + "F14", {"entities" : qUnion([Q0, Q1, Q2, Q3, Q4, Q5]), "radius" : 3 * mm, "tangentPropagation" : true, "allowEdgeOverflow" : false});
        }
        {
            var Q0;
            Q0=makeQuery(id+"F1.opExtrude","CAP_EDGE",EDGE,{"disambiguationData":[OSD([sQuery(id+"F0.wireOp",EDGE,"E1.bottom")])],"isStart":false});
            fillet(context, id + "F15", {"entities" : qUnion([Q0]), "radius" : 2 * mm, "tangentPropagation" : true, "allowEdgeOverflow" : false});
        }
        {
            var Q0;
            {var subQ0=sQuery(id+"F0.wireOp",EDGE,"E21.filletArc");var subQ1=sQuery(id+"F0.wireOp",EDGE,"E7");var subQ2=sQuery(id+"F0.wireOp",EDGE,"E6");var subQ3=sQuery(id+"F0.wireOp",EDGE,"E5");var subQ4=sQuery(id+"F0.wireOp",EDGE,"E4");var subQ5=sQuery(id+"F0.wireOp",EDGE,"E22.filletArc");var subQ6=sQuery(id+"F0.wireOp",EDGE,"E1.bottom");var subQ7=sQuery(id+"F0.wireOp",EDGE,"E1.right");var subQ8=sQuery(id+"F0.wireOp",EDGE,"E1.top");var subQ9=sQuery(id+"F0.wireOp",EDGE,"E1.left");var subQ10=sQuery(id+"F0.wireOp",EDGE,"E23.filletArc");var subQ11=sQuery(id+"F0.wireOp",EDGE,"E24.filletArc");Q0=makeQuery(id+"F2.boolean.opBoolean","SPLIT",FACE,{"disambiguationData":[TD([makeQuery(id+"F1.opExtrude","SWEPT_FACE",FACE,{"disambiguationData":[OSD([subQ6])]})])],"derivedFrom":makeQuery(id+"F1.opExtrude","CAP_FACE",FACE,{"disambiguationData":[OSD([subQ6,subQ8,subQ9,subQ7,subQ4,subQ3,subQ2,subQ1,subQ0,subQ5,subQ10,subQ11])],"isStart":true})});}
            var sketch = newSketch(context, id + "F16", { "sketchPlane" : qUnion([Q0])});
            skLineSegment(sketch, "E79.0", {"start": v(-80, -80) * mm, "end": v(-80, 80) * mm});
            skArc(sketch, "E79.1", {"start": v(-70, 90) * mm, "mid": v(-77.07, 87.07) * mm, "end": v(-80, 80) * mm});
            skLineSegment(sketch, "E79.2", {"start": v(-70, 90) * mm, "end": v(70, 90) * mm});
            skArc(sketch, "E79.3", {"start": v(80, 80) * mm, "mid": v(77.07, 87.07) * mm, "end": v(70, 90) * mm});
            skLineSegment(sketch, "E79.4", {"start": v(80, -80) * mm, "end": v(80, 80) * mm});
            skArc(sketch, "E79.5", {"start": v(70, -90) * mm, "mid": v(77.07, -87.07) * mm, "end": v(80, -80) * mm});
            skLineSegment(sketch, "E79.6", {"start": v(-70, -90) * mm, "end": v(70, -90) * mm});
            skArc(sketch, "E79.7", {"start": v(-80, -80) * mm, "mid": v(-77.07, -87.07) * mm, "end": v(-70, -90) * mm});
            skCircle(sketch, "E79.8", {"center": v(-60, -67.5) * mm, "radius": 4 * mm});
            skCircle(sketch, "E79.9", {"center": v(60, -67.5) * mm, "radius": 4 * mm});
            skCircle(sketch, "E79.10", {"center": v(60, 67.5) * mm, "radius": 4 * mm});
            skCircle(sketch, "E79.11", {"center": v(-60, 67.5) * mm, "radius": 4 * mm});
            skArc(sketch, "E79.12", {"start": v(56.15, 48.18) * mm, "mid": v(0, 67.5) * mm, "end": v(-56.15, 48.18) * mm});
            skArc(sketch, "E79.13", {"start": v(-56.15, 48.18) * mm, "mid": v(-58.99, 44.68) * mm, "end": v(-60, 40.3) * mm});
            skLineSegment(sketch, "E79.14", {"start": v(-60, 40.3) * mm, "end": v(-60, -40.3) * mm});
            skArc(sketch, "E79.15", {"start": v(-60, -40.3) * mm, "mid": v(-58.99, -44.68) * mm, "end": v(-56.15, -48.18) * mm});
            skArc(sketch, "E79.16", {"start": v(-56.15, -48.18) * mm, "mid": v(0, -67.5) * mm, "end": v(56.15, -48.18) * mm});
            skArc(sketch, "E79.17", {"start": v(56.15, -48.18) * mm, "mid": v(58.99, -44.68) * mm, "end": v(60, -40.3) * mm});
            skLineSegment(sketch, "E79.18", {"start": v(60, 40.3) * mm, "end": v(60, -40.3) * mm});
            skArc(sketch, "E79.19", {"start": v(60, 40.3) * mm, "mid": v(58.99, 44.68) * mm, "end": v(56.15, 48.18) * mm});
            skLineSegment(sketch, "E80", {"start": v(0, 90) * mm, "end": v(0, 120) * mm, "construction": true});
            skCircle(sketch, "E81", {"center": v(0, 120) * mm, "radius": 6 * mm});
            skArc(sketch, "E82", {"start": v(15, 120) * mm, "mid": v(0, 135) * mm, "end": v(-15, 120) * mm});
            skLineSegment(sketch, "E83", {"start": v(-15, 120) * mm, "end": v(-15, 108) * mm});
            skLineSegment(sketch, "E84", {"start": v(-15, 108) * mm, "end": v(-33, 90) * mm});
            skLineSegment(sketch, "E85", {"start": v(15, 120) * mm, "end": v(15, 108) * mm});
            skLineSegment(sketch, "E86", {"start": v(15, 108) * mm, "end": v(33, 90) * mm});
            skLineSegment(sketch, "E87", {"start": v(-80, 0) * mm, "end": v(80, 0) * mm, "construction": true});
            skLineSegment(sketch, "E88.MirrorCS", {"start": v(-15, -120) * mm, "end": v(-15, -108) * mm});
            skLineSegment(sketch, "E89.MirrorCS", {"start": v(15, -120) * mm, "end": v(15, -108) * mm});
            skLineSegment(sketch, "E90.MirrorCS", {"start": v(15, -108) * mm, "end": v(33, -90) * mm});
            skCircle(sketch, "E91.MirrorC", {"center": v(0, -120) * mm, "radius": 6 * mm});
            skLineSegment(sketch, "E92.MirrorCS", {"start": v(0, -90) * mm, "end": v(0, -120) * mm, "construction": true});
            skArc(sketch, "E93.MirrorCS", {"start": v(15, -120) * mm, "mid": v(0, -135) * mm, "end": v(-15, -120) * mm});
            skLineSegment(sketch, "E94.MirrorCS", {"start": v(-15, -108) * mm, "end": v(-33, -90) * mm});
            skSolve(sketch);
        }
        {
            var Q0;
            Q0=makeQuery(id+"F16.imprint","IMPRINT",FACE,{"disambiguationData":[TD([[makeQuery(id+"F16.imprint","IMPRINT",EDGE,{"derivedFrom":sQuery(id+"F16.wireOp",EDGE,"E81")}),-1.0]])]});
            var Q1;
            Q1=makeQuery(id+"F16.imprint","IMPRINT",FACE,{"disambiguationData":[TD([[makeQuery(id+"F16.imprint","IMPRINT",EDGE,{"derivedFrom":sQuery(id+"F16.wireOp",EDGE,"E88.MirrorCS")}),-1.0]])]});
            var Q2;
            Q2=makeQuery(id+"F16.imprint","IMPRINT",FACE,{"disambiguationData":[TD([[makeQuery(id+"F16.imprint","IMPRINT",EDGE,{"derivedFrom":sQuery(id+"F16.wireOp",EDGE,"E79.0")}),-1.0]])]});
            var Q3;
            Q3=makeQuery(id+"F2.opExtrude","CAP_FACE",FACE,{"disambiguationData":[OSD([sQuery(id+"F0.wireOp",EDGE,"E12"),sQuery(id+"F0.wireOp",EDGE,"E13"),sQuery(id+"F0.wireOp",EDGE,"E14"),sQuery(id+"F0.wireOp",EDGE,"E15"),sQuery(id+"F0.wireOp",EDGE,"E17.filletArc"),sQuery(id+"F0.wireOp",EDGE,"E18.filletArc"),sQuery(id+"F0.wireOp",EDGE,"E19.filletArc"),sQuery(id+"F0.wireOp",EDGE,"E20.filletArc"),sQuery(id+"F0.wireOp",EDGE,"E25.0"),sQuery(id+"F0.wireOp",EDGE,"E25.1"),sQuery(id+"F0.wireOp",EDGE,"E25.2"),sQuery(id+"F0.wireOp",EDGE,"E25.3"),sQuery(id+"F0.wireOp",EDGE,"E25.4"),sQuery(id+"F0.wireOp",EDGE,"E25.5"),sQuery(id+"F0.wireOp",EDGE,"E25.6"),sQuery(id+"F0.wireOp",EDGE,"E25.7")])],"isStart":false});
            extrude(context, id + "F17", {"entities" : qUnion([Q0, Q1, Q2]), "endBound" : BoundingType.UP_TO_SURFACE, "depth" : 25 * mm, "endBoundEntityFace" : qUnion([Q3]), "offsetDistance" : 25 * mm});
        }
    });
